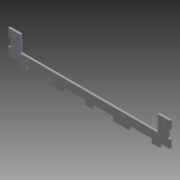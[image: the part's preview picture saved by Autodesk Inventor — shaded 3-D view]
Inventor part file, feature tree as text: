
AUTODESK INVENTOR PART (.ipt)
format: ipt  version: 2011 (Build 150239000, 239)  size: 779,776 bytes
history: native  units: in
note: dims shown in document units (in); Inventor stores cm internally (conversion verified against a paired STEP export)
features: extrude x28, sketch x28, fillet x2
ambient origin geometry x8: Origin, YZ Plane, XZ Plane, XY Plane, X Axis, Y Axis, Z Axis, Center Point
bodies: Solid1 (feature_tree)
feature tree (58):
  extrude  "Extrusion1"  Depth=41.5in
  extrude  "Extrusion2"  Depth=10.0in
  extrude  "Extrusion3"  Depth=0.6in
  extrude  "Extrusion4"  Depth=0.25in
  extrude  "Extrusion5"  Depth=0.5in
  extrude  "Extrusion6"  Depth=1.0in
  extrude  "Extrusion7"  Depth=4.1in TaperAngle=0.0deg
  extrude  "Extrusion8"  Depth=1.0in
  extrude  "Extrusion9"  Depth=1.0in
  extrude  "Extrusion10"  Depth=1.0in
  extrude  "Extrusion11"  Depth=4.1in TaperAngle=0.0deg
  extrude  "Extrusion12"  Depth=0.5in
  fillet  "Fillet1"  Radius=0.25in
  fillet  "Fillet2"  Radius=1.0in
  extrude  "Extrusion13"  Depth=3.0in
  extrude  "Extrusion14"  Depth=3.0in
  extrude  "Extrusion15"  Depth=3.0in
  extrude  "Extrusion16"  Depth=3.0in
  extrude  "Extrusion17"  Depth=3.0in
  extrude  "Extrusion18"  Depth=0.25in
  extrude  "Extrusion19"  Depth=0.25in TaperAngle=0.0deg
  extrude  "Extrusion20"  Depth=0.25in
  extrude  "Extrusion21"  Depth=1.0in
  extrude  "Extrusion22"  Depth=1.0in
  extrude  "Extrusion23"  Depth=0.156in
  extrude  "Extrusion24"  Depth=0.156in
  extrude  "Extrusion25"  Depth=0.25in TaperAngle=0.0deg
  extrude  "Extrusion26"  Depth=0.25in TaperAngle=0.0deg
  extrude  "Extrusion27"  Depth=1.0in
  extrude  "Extrusion28"  Depth=1.0in
  sketch  "Sketch1"  dims[d0=20.0in d1=41.5in]
  sketch  "Sketch2"  dims[d2=0.25in d3=0.0in d4=10.0in]
  sketch  "Sketch3"  dims[d5=0.25in d6=0.6in]
  sketch  "Sketch4"  dims[d7=1.2in d8=0.25in]
  sketch  "Sketch5"  dims[d9=4.1in d10=0.0in d11=0.5in]
  sketch  "Sketch6"  dims[d12=0.5in d13=1.0in]
  sketch  "Sketch7"  dims[d14=1.0in d15=4.1in d16=0.0in]
  sketch  "Sketch8"  dims[d17=1.0in d18=1.0in]
  sketch  "Sketch9"  dims[d19=1.0in d20=1.0in]
  sketch  "Sketch10"  dims[d21=6.75in d22=1.0in]
  sketch  "Sketch11"  dims[d23=0.5in d24=4.1in d25=0.0in]
  sketch  "Sketch12"  dims[d26=0.25in d27=0.5in d28=0.25in d29=0.0in d30=1.0in]
  sketch  "Sketch13"  dims[d31=1.0in d32=3.0in]
  sketch  "Sketch14"  dims[d33=1.0in d34=3.0in]
  sketch  "Sketch15"  dims[d35=1.0in d36=3.0in]
  sketch  "Sketch16"  dims[d37=1.0in d38=3.0in]
  sketch  "Sketch17"  dims[d39=1.0in d40=3.0in]
  sketch  "Sketch18"  dims[d41=1.0in d42=0.25in]
  sketch  "Sketch19"  dims[d43=1.0in d44=0.0in d45=0.25in d46=0.0in]
  sketch  "Sketch20"  dims[d47=1.0in d48=0.25in]
  sketch  "Sketch21"  dims[d49=1.0in d50=1.0in]
  sketch  "Sketch22"  dims[d51=1.0in d52=1.0in]
  sketch  "Sketch23"  dims[d53=0.25in d54=0.0in d55=0.156in]
  sketch  "Sketch24"  dims[d56=0.156in d57=0.156in]
  sketch  "Sketch25"  dims[d58=0.156in d59=0.25in d60=0.0in]
  sketch  "Sketch26"  dims[d61=0.25in d62=0.0in d63=0.25in d64=0.0in]
  sketch  "Sketch27"  dims[d65=1.0in d66=1.0in]
  sketch  "Sketch28"  dims[d67=1.0in d68=1.0in d69=1.0in d70=1.0in d71=1.0in d72=1.0in d73=0.25in d74=0.0in d75=0.5in d76=0.5in d77=1.0in d78=0.0in d79=3.0in d80=3.0in d81=0.25in d82=0.0in d83=0.75in d84=0.75in d85=0.75in d86=0.75in d87=0.156in d88=0.156in d89=0.25in d90=0.0in d91=0.25in d92=1.0in d93=1.0in d94=1.0in d95=0.25in d96=0.0in d97=0.25in d98=1.0in d99=1.0in d100=1.0in d101=0.25in d102=0.0in d103=1.0in d104=0.0in d105=0.75in d106=0.5in d107=0.156in d108=0.156in d109=1.0in d110=0.0in d111=0.25in d112=0.0in d113=0.5in d114=0.5in d115=1.0in d116=0.25in d117=1.0in d118=1.0in d119=1.0in d120=1.0in d121=1.0in d122=1.0in d123=1.0in d124=1.0in d125=1.0in d126=1.0in d127=1.0in d128=1.0in d129=1.0in d130=1.0in d131=1.0in d132=1.0in d133=1.0in d134=1.0in d135=0.25in d136=0.0in d137=0.25in d138=0.0in d139=1.0in d140=0.0in d141=1.25in d142=1.0in d143=0.25in d144=1.0in d145=0.25in d146=1.0in d147=3.25in d148=1.0in d149=3.0in d150=1.0in d151=1.0in d152=2.0in d153=1.0in d154=0.25in d155=0.0in d156=0.25in d157=0.25in d158=0.0in d159=0.25in d160=0.0in d161=0.5in d162=0.5in d163=2.0in d164=2.0in d165=0.25in d166=0.0in d167=1.25in d168=0.5in d169=1.25in d170=0.5in d171=0.25in d172=0.0in]
